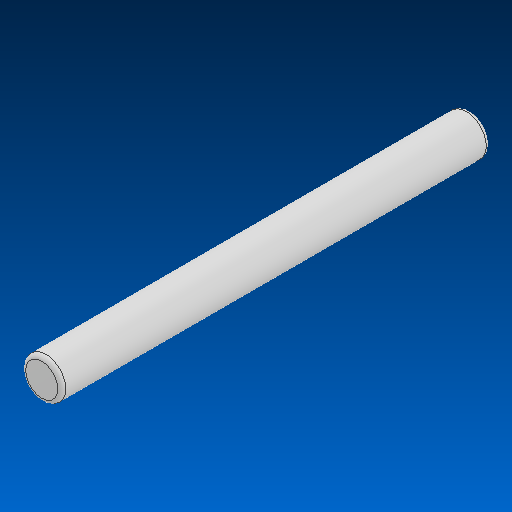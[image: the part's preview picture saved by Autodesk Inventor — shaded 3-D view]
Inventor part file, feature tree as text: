
AUTODESK INVENTOR PART (.ipt)
format: ipt  version: 2022.2 (Build 262287000, 287)  size: 94,720 bytes
history: native  units: in
note: dims shown in document units (in); Inventor stores cm internally (conversion verified against a paired STEP export)
features: fillet x1
ambient origin geometry x8: Origin, YZ Plane, XZ Plane, XY Plane, X Axis, Y Axis, Z Axis, Center Point
bodies: Solid1 (feature_tree)
feature tree (1):
  fillet  "Fillet1"  [1 undecoded]
note: 1 required parameter value undecoded (feature->parameter linkage not recoverable at this tier; creation-order binding heuristic only, values carry confidence <= 0.55)
